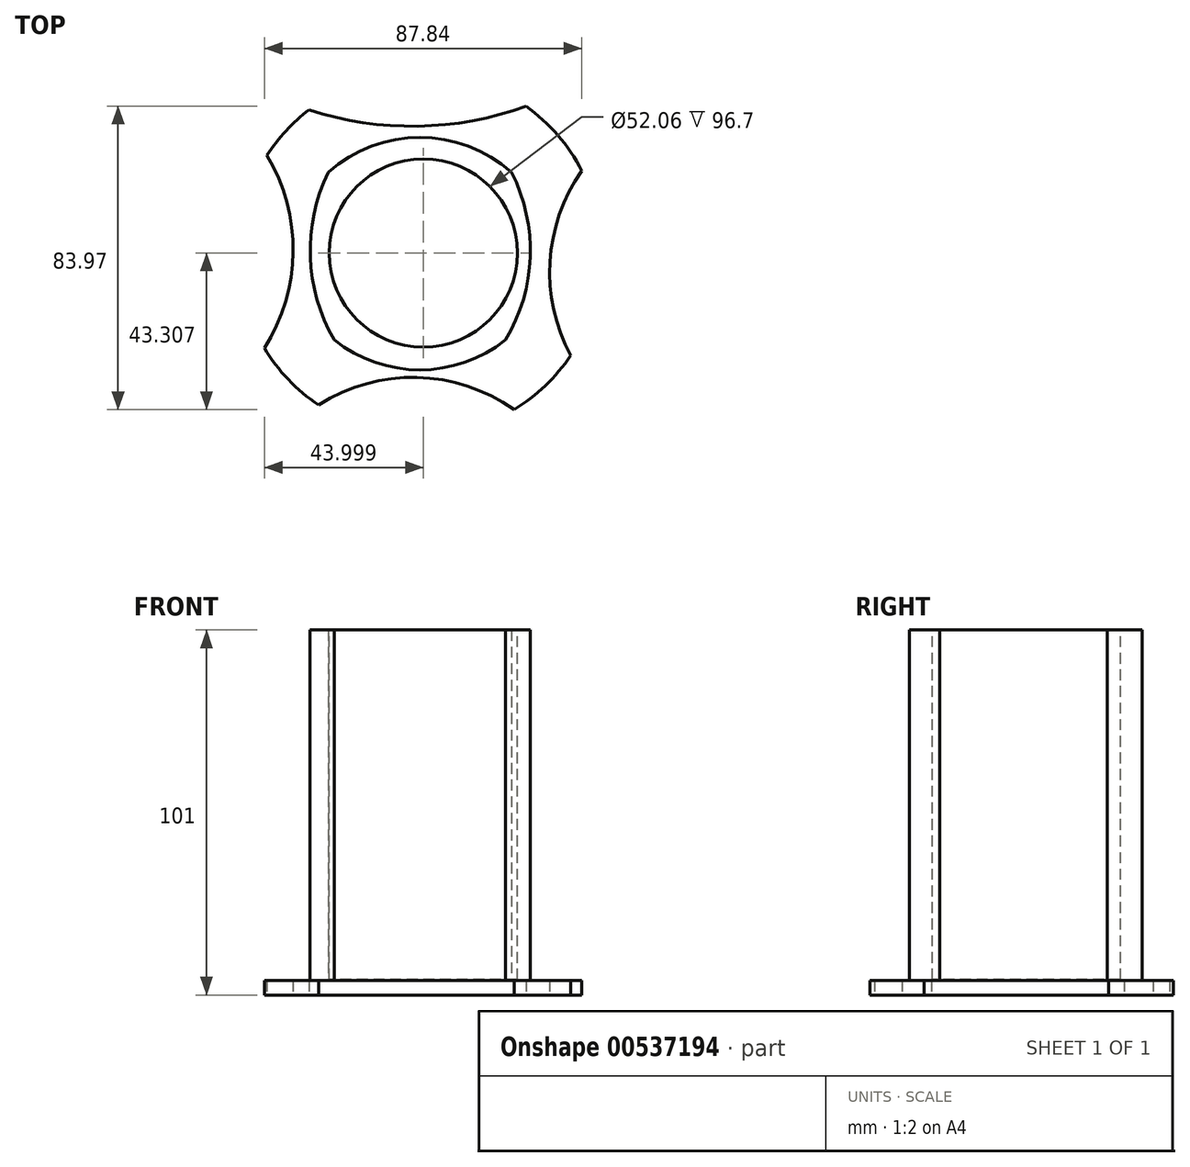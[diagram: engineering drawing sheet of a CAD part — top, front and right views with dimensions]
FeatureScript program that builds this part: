
annotation { "Feature Type Name" : "Feature", "Feature Type Description" : "" }
export const myFeature = defineFeature(function(context is Context, id is Id, definition is map)
    precondition{}
    {
        {
            var Q0;
            Q0=qCreatedBy(makeId("Top.planeOp"),FACE);
            var sketch = newSketch(context, id + "F0", { "sketchPlane" : qUnion([Q0])});
            skCircle(sketch, "E0", {"center": v(0, 0) * mm, "radius": 37.54 * mm});
            skArc(sketch, "E1", {"start": v(37.54, 0) * mm, "mid": v(0, 32.27) * mm, "end": v(-37.54, 0) * mm});
            skArc(sketch, "E2", {"start": v(-37.54, 0) * mm, "mid": v(0, -32.1) * mm, "end": v(37.54, 0) * mm});
            skArc(sketch, "E3", {"start": v(-25.38, 22.54) * mm, "mid": v(-30.34, -0.85) * mm, "end": v(-23.7, -23.8) * mm});
            skArc(sketch, "E4", {"start": v(23.7, -23.8) * mm, "mid": v(30.51, -0.85) * mm, "end": v(25.38, 22.54) * mm});
            skCircle(sketch, "E5", {"center": v(-2.13, 0) * mm, "radius": 64.81 * mm});
            skSolve(sketch);
        }
        {
            var Q0;
            {var subQ0=sQuery(id+"F0.wireOp",EDGE,"E3");Q0=makeQuery(id+"F0.imprint","IMPRINT",FACE,{"disambiguationData":[TD([[makeQuery(id+"F0.imprint","IMPRINT",EDGE,{"derivedFrom":subQ0}),1.0]])]});}
            extrude(context, id + "F1", {"entities" : qUnion([Q0]), "depth" : 101 * mm, "offsetDistance" : 25 * mm});
        }
        {
            var Q0;
            Q0=makeQuery(id+"F1.opExtrude","CAP_FACE",FACE,{"disambiguationData":[OSD([sQuery(id+"F0.wireOp",EDGE,"E1"),sQuery(id+"F0.wireOp",EDGE,"E2"),sQuery(id+"F0.wireOp",EDGE,"E3"),sQuery(id+"F0.wireOp",EDGE,"E4")])],"isStart":false});
            var sketch = newSketch(context, id + "F2", { "sketchPlane" : qUnion([Q0])});
            skCircle(sketch, "E6", {"center": v(0.95, 0.24) * mm, "radius": 26.03 * mm});
            skSolve(sketch);
        }
        {
            var Q0;
            Q0=makeQuery(id+"F2.imprint","IMPRINT",FACE,{"disambiguationData":[TD([[makeQuery(id+"F2.imprint","IMPRINT",EDGE,{"derivedFrom":sQuery(id+"F2.wireOp",EDGE,"E6")}),1.0]])]});
            extrude(context, id + "F3", {"entities" : qUnion([Q0]), "operationType" : NewBodyOperationType.REMOVE, "oppositeDirection" : true, "depth" : 96.7 * mm, "offsetDistance" : 25 * mm});
        }
        {
            var Q0;
            Q0=qCreatedBy(makeId("Top.planeOp"),FACE);
            var sketch = newSketch(context, id + "F4", { "sketchPlane" : qUnion([Q0])});
            skCircle(sketch, "E7", {"center": v(0, 0) * mm, "radius": 50.33 * mm});
            skArc(sketch, "E8", {"start": v(-30.69, 39.9) * mm, "mid": v(-0.59, 35.34) * mm, "end": v(29.34, 40.9) * mm});
            skArc(sketch, "E9", {"start": v(44.79, 22.97) * mm, "mid": v(35.98, -2.13) * mm, "end": v(41.77, -28.09) * mm});
            skArc(sketch, "E10", {"start": v(26.05, -43.07) * mm, "mid": v(-0.8, -34.16) * mm, "end": v(-28.06, -41.79) * mm});
            skArc(sketch, "E11", {"start": v(-43.05, -26.08) * mm, "mid": v(-35.08, 0.48) * mm, "end": v(-42.32, 27.25) * mm});
            skSolve(sketch);
        }
        {
            var Q0;
            Q0=makeQuery(id+"F4.imprint","IMPRINT",FACE,{"disambiguationData":[TD([[makeQuery(id+"F4.imprint","IMPRINT",EDGE,{"derivedFrom":sQuery(id+"F4.wireOp",EDGE,"E7")}),1.0]])]});
            extrude(context, id + "F5", {"entities" : qUnion([Q0]), "operationType" : NewBodyOperationType.ADD, "depth" : 4 * mm, "offsetDistance" : 25 * mm});
        }
    });
